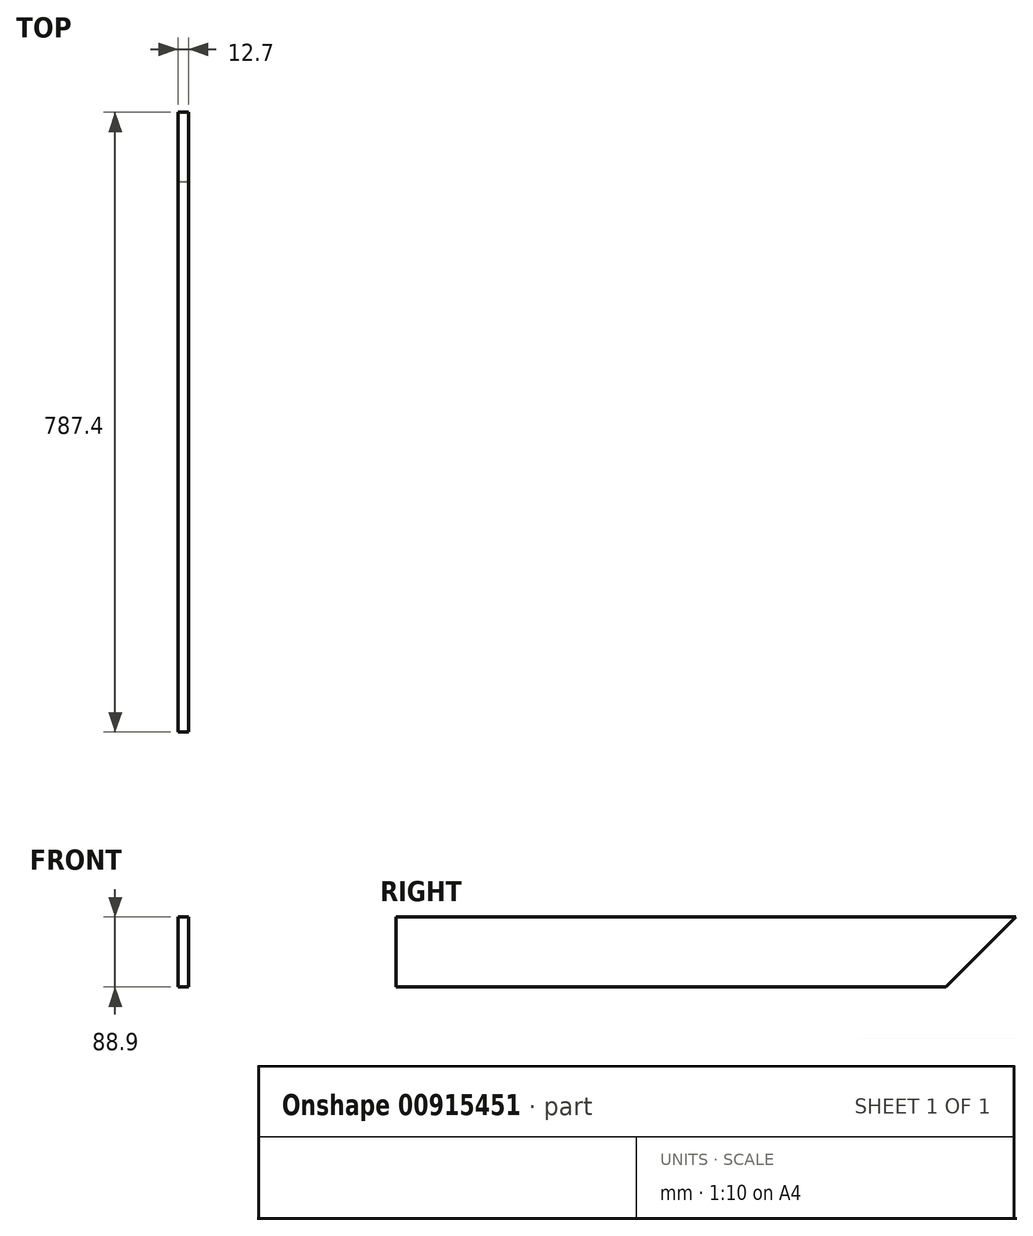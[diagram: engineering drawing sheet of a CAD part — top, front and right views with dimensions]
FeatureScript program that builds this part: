
annotation { "Feature Type Name" : "Feature", "Feature Type Description" : "" }
export const myFeature = defineFeature(function(context is Context, id is Id, definition is map)
    precondition{}
    {
        {
            var Q0;
            Q0=qCreatedBy(makeId("Right.planeOp"),FACE);
            var sketch = newSketch(context, id + "F0", { "sketchPlane" : qUnion([Q0])});
            skLineSegment(sketch, "E0.bottom", {"start": v(-393.7, 44.45) * mm, "end": v(393.7, 44.45) * mm});
            skLineSegment(sketch, "E0.top", {"start": v(-393.7, -44.45) * mm, "end": v(304.8, -44.45) * mm});
            skLineSegment(sketch, "E0.left", {"start": v(-393.7, 44.45) * mm, "end": v(-393.7, -44.45) * mm});
            skPoint(sketch, "E0.middle", {"position": v(0, 0) * mm});
            skLineSegment(sketch, "E1", {"start": v(393.7, 44.45) * mm, "end": v(304.8, -44.45) * mm});
            skSolve(sketch);
        }
        {
            var Q0;
            Q0=makeQuery(id+"F0.imprint","IMPRINT",FACE,{"disambiguationData":[TD([[makeQuery(id+"F0.imprint","IMPRINT",EDGE,{"derivedFrom":sQuery(id+"F0.wireOp",EDGE,"E0.bottom")}),-1.0]])]});
            extrude(context, id + "F1", {"entities" : qUnion([Q0]), "depth" : 12.7 * mm, "offsetDistance" : 25.4 * mm});
        }
    });
